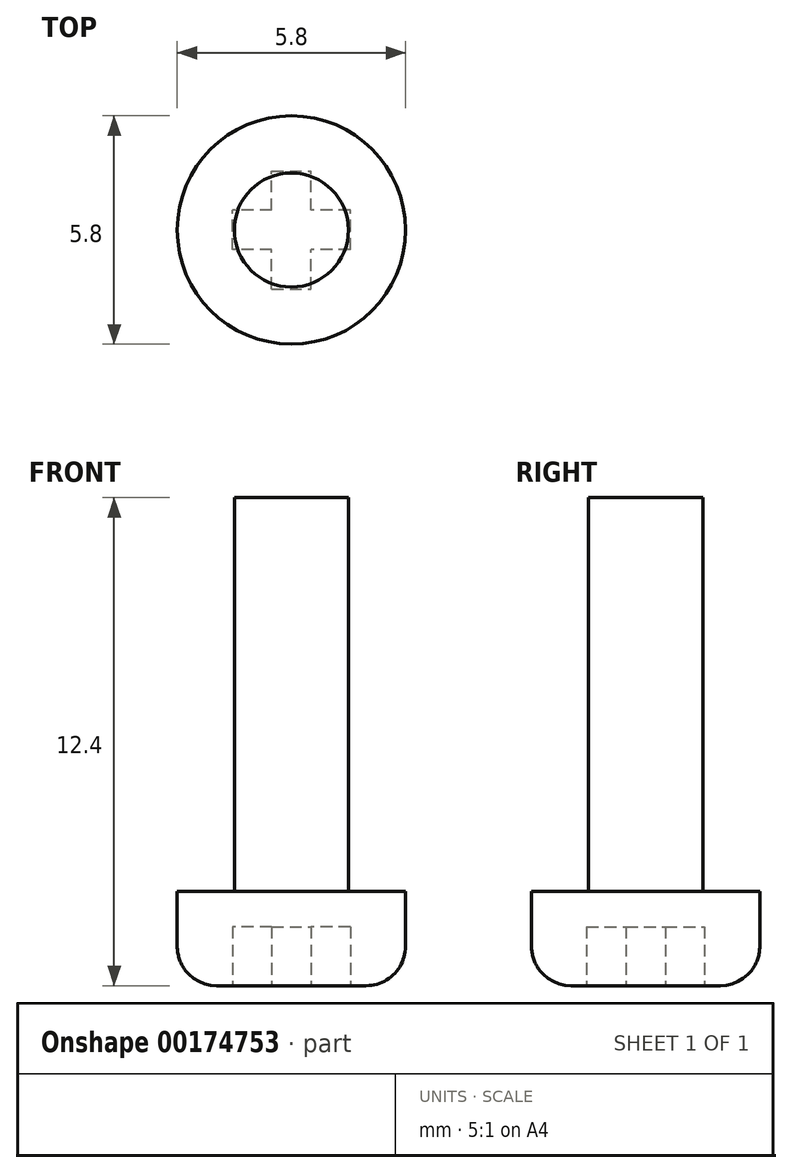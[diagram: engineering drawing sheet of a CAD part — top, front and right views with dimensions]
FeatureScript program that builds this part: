
annotation { "Feature Type Name" : "Feature", "Feature Type Description" : "" }
export const myFeature = defineFeature(function(context is Context, id is Id, definition is map)
    precondition{}
    {
        {
            var Q0;
            Q0=qCreatedBy(makeId("Top.planeOp"),FACE);
            var sketch = newSketch(context, id + "F0", { "sketchPlane" : qUnion([Q0])});
            skCircle(sketch, "E0", {"center": v(0, 0) * mm, "radius": 1.45 * mm});
            skSolve(sketch);
        }
        {
            var Q0;
            Q0=qSketchRegion(id+"F0",true);
            extrude(context, id + "F1", {"entities" : qUnion([Q0]), "depth" : 10 * mm});
        }
        {
            var Q0;
            Q0=qCreatedBy(makeId("Top.planeOp"),FACE);
            var sketch = newSketch(context, id + "F2", { "sketchPlane" : qUnion([Q0])});
            skCircle(sketch, "E1", {"center": v(0, 0) * mm, "radius": 2.9 * mm});
            skSolve(sketch);
        }
        {
            var Q0;
            Q0=qSketchRegion(id+"F2",true);
            extrude(context, id + "F3", {"entities" : qUnion([Q0]), "operationType" : NewBodyOperationType.ADD, "oppositeDirection" : true, "depth" : 2.4 * mm});
        }
        {
            var Q0;
            Q0=makeQuery(id+"F3.opExtrude","CAP_EDGE",EDGE,{"disambiguationData":[OSD([sQuery(id+"F2.wireOp",EDGE,"E1")])],"isStart":false});
            fillet(context, id + "F4", {"entities" : qUnion([Q0]), "radius" : 1 * mm, "tangentPropagation" : true, "allowEdgeOverflow" : false});
        }
        {
            var Q0;
            Q0=makeQuery(id+"F3.opExtrude","CAP_FACE",FACE,{"disambiguationData":[OSD([sQuery(id+"F2.wireOp",EDGE,"E1")])],"isStart":false});
            var sketch = newSketch(context, id + "F5", { "sketchPlane" : qUnion([Q0])});
            skLineSegment(sketch, "E2.bottom", {"start": v(1.5, 0.5) * mm, "end": v(-1.5, 0.5) * mm});
            skLineSegment(sketch, "E2.top", {"start": v(1.5, -0.5) * mm, "end": v(-1.5, -0.5) * mm});
            skLineSegment(sketch, "E2.left", {"start": v(1.5, 0.5) * mm, "end": v(1.5, -0.5) * mm});
            skLineSegment(sketch, "E2.right", {"start": v(-1.5, 0.5) * mm, "end": v(-1.5, -0.5) * mm});
            skPoint(sketch, "E2.middle", {"position": v(0, 0) * mm});
            skLineSegment(sketch, "E3.bottom", {"start": v(-0.5, 1.5) * mm, "end": v(0.5, 1.5) * mm});
            skLineSegment(sketch, "E3.top", {"start": v(-0.5, -1.5) * mm, "end": v(0.5, -1.5) * mm});
            skLineSegment(sketch, "E3.left", {"start": v(-0.5, 1.5) * mm, "end": v(-0.5, -1.5) * mm});
            skLineSegment(sketch, "E3.right", {"start": v(0.5, 1.5) * mm, "end": v(0.5, -1.5) * mm});
            skSolve(sketch);
        }
        {
            var Q0;
            Q0=qSketchRegion(id+"F5",true);
            extrude(context, id + "F6", {"entities" : qUnion([Q0]), "operationType" : NewBodyOperationType.REMOVE, "oppositeDirection" : true, "depth" : 1.5 * mm});
        }
    });
